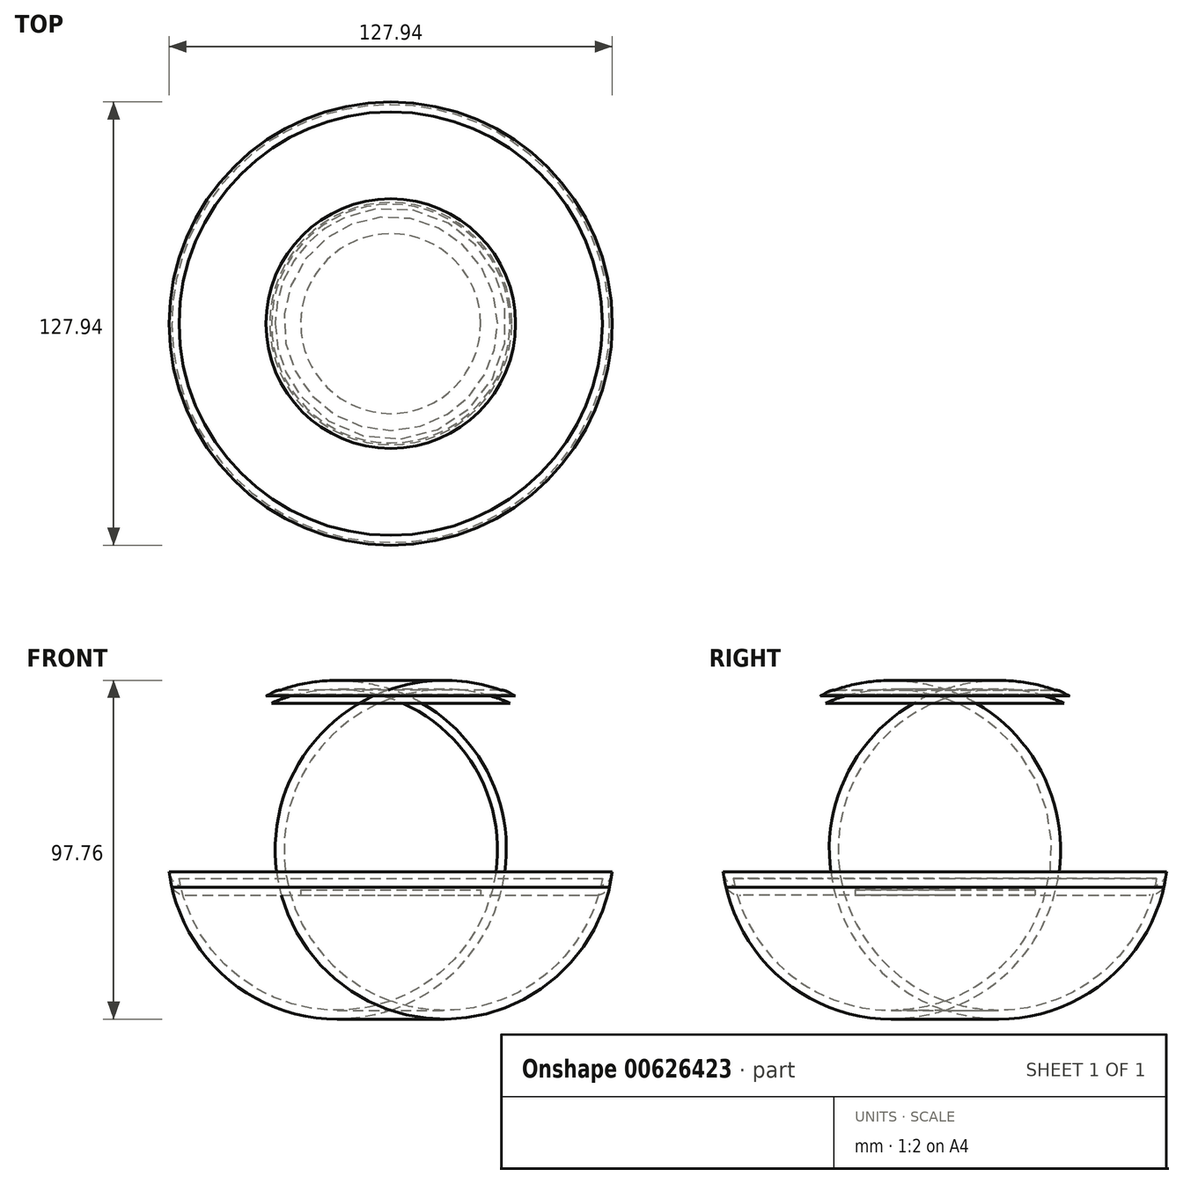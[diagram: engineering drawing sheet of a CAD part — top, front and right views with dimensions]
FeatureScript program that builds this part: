
annotation { "Feature Type Name" : "Feature", "Feature Type Description" : "" }
export const myFeature = defineFeature(function(context is Context, id is Id, definition is map)
    precondition{}
    {
        {
            var Q0;
            Q0=qCreatedBy(makeId("Front.planeOp"),FACE);
            var sketch = newSketch(context, id + "F0", { "sketchPlane" : qUnion([Q0])});
            skLineSegment(sketch, "E0", {"start": v(-34.97, 0) * mm, "end": v(37.56, 0) * mm});
            skLineSegment(sketch, "E1", {"start": v(-63.17, -55.7) * mm, "end": v(68.93, -55.7) * mm});
            skArc(sketch, "E2", {"start": v(-34.97, 0) * mm, "mid": v(-59.12, -22.76) * mm, "end": v(-63.17, -55.7) * mm});
            skArc(sketch, "E3", {"start": v(68.93, -55.7) * mm, "mid": v(64.02, -21.78) * mm, "end": v(37.56, 0) * mm});
            skLineSegment(sketch, "E4", {"start": v(0, 0) * mm, "end": v(0, -55.7) * mm});
            skSolve(sketch);
        }
        {
            var Q0;
            {var subQ0=sQuery(id+"F0.wireOp",EDGE,"E2");Q0=makeQuery(id+"F0.imprint","IMPRINT",FACE,{"disambiguationData":[TD([[makeQuery(id+"F0.imprint","IMPRINT",EDGE,{"derivedFrom":subQ0}),1.0]])]});}
            var Q1;
            Q1=sQuery(id+"F0.wireOp",EDGE,"E4");
            revolve(context, id + "F1", {"entities" : qUnion([Q0]), "axis" : qUnion([Q1]), "revolveType" : RevolveType.FULL});
        }
        {
            var Q0;
            Q0=makeQuery(id+"F1.opRevolve","SWEPT_FACE",FACE,{"disambiguationData":[OSD([sQuery(id+"F0.wireOp",EDGE,"E0")])]});
            var sketch = newSketch(context, id + "F2", { "sketchPlane" : qUnion([Q0])});
            skCircle(sketch, "E5", {"center": v(0, 0) * mm, "radius": 34.94 * mm});
            skSolve(sketch);
        }
        {
            var Q0;
            Q0=makeQuery(id+"F2.imprint","IMPRINT",FACE,{"disambiguationData":[TD([[makeQuery(id+"F2.imprint","IMPRINT",EDGE,{"derivedFrom":sQuery(id+"F2.wireOp",EDGE,"E5")}),1.0]])]});
            extrude(context, id + "F3", {"entities" : qUnion([Q0]), "depth" : 1.27 * mm, "offsetDistance" : 25.4 * mm});
        }
        {
            var Q0;
            Q0=makeQuery(id+"F1.opRevolve","SWEPT_FACE",FACE,{"disambiguationData":[OSD([sQuery(id+"F0.wireOp",EDGE,"E1")])]});
            var sketch = newSketch(context, id + "F4", { "sketchPlane" : qUnion([Q0])});
            skCircle(sketch, "E6", {"center": v(0, 0) * mm, "radius": 63.53 * mm});
            skSolve(sketch);
        }
        {
            var Q0;
            Q0=makeQuery(id+"F4.imprint","IMPRINT",FACE,{"disambiguationData":[TD([[makeQuery(id+"F4.imprint","IMPRINT",EDGE,{"derivedFrom":makeQuery(id+"F1.opRevolve","SWEPT_EDGE",EDGE,{"disambiguationData":[OSD([sQuery(id+"F0.wireOp",EDGE,"E1"),sQuery(id+"F0.wireOp",EDGE,"E2")])]})}),-1.0]])]});
            extrude(context, id + "F5", {"entities" : qUnion([Q0]), "depth" : 2.3 * mm, "offsetDistance" : 25.4 * mm});
        }
        {
            var Q0;
            Q0=makeQuery(id+"F1.opRevolve","SWEPT_FACE",FACE,{"disambiguationData":[OSD([sQuery(id+"F0.wireOp",EDGE,"E2")])]});
            var Q1;
            Q1=makeQuery(id+"F1.opRevolve","SWEPT_BODY",BODY,{"disambiguationData":[OSD([sQuery(id+"F0.wireOp",EDGE,"E0"),sQuery(id+"F0.wireOp",EDGE,"E1"),sQuery(id+"F0.wireOp",EDGE,"E2"),sQuery(id+"F0.wireOp",EDGE,"E4")])]});
            shell(context, id + "F6", {"isHollow" : true, "entities" : qUnion([Q0]), "parts" : qUnion([Q1]), "thickness" : 2.54 * mm});
        }
        {
            var Q0;
            Q0=makeQuery(id+"F5.opExtrude","CAP_EDGE",EDGE,{"disambiguationData":[OSD([sQuery(id+"F0.wireOp",EDGE,"E1"),sQuery(id+"F0.wireOp",EDGE,"E2")])],"isStart":false});
            var Q1;
            Q1=makeQuery(id+"F3.opExtrude","CAP_EDGE",EDGE,{"disambiguationData":[OSD([sQuery(id+"F2.wireOp",EDGE,"E5")])],"isStart":false});
            var Q2;
            Q2=makeQuery(id+"F1.opRevolve","SWEPT_EDGE",EDGE,{"disambiguationData":[OSD([sQuery(id+"F0.wireOp",EDGE,"E0"),sQuery(id+"F0.wireOp",EDGE,"E2")])]});
            var Q3;
            Q3=makeQuery(id+"F1.opRevolve","SWEPT_EDGE",EDGE,{"disambiguationData":[OSD([sQuery(id+"F0.wireOp",EDGE,"E1"),sQuery(id+"F0.wireOp",EDGE,"E2")])]});
            fillet(context, id + "F7", {"entities" : qUnion([Q0, Q1, Q2, Q3]), "radius" : 5.08 * mm, "tangentPropagation" : true, "allowEdgeOverflow" : false});
        }
        {
            var Q0;
            Q0=makeQuery(id+"F5.opExtrude","CAP_FACE",FACE,{"disambiguationData":[OSD([sQuery(id+"F0.wireOp",EDGE,"E1"),sQuery(id+"F0.wireOp",EDGE,"E2")])],"isStart":false});
            var sketch = newSketch(context, id + "F8", { "sketchPlane" : qUnion([Q0])});
            skCircle(sketch, "E7", {"center": v(0, 0) * mm, "radius": 25.97 * mm});
            skSolve(sketch);
        }
        {
            var Q0;
            Q0=makeQuery(id+"F8.imprint","IMPRINT",FACE,{"disambiguationData":[TD([[makeQuery(id+"F8.imprint","IMPRINT",EDGE,{"derivedFrom":sQuery(id+"F8.wireOp",EDGE,"E7")}),1.0]])]});
            extrude(context, id + "F9", {"entities" : qUnion([Q0]), "operationType" : NewBodyOperationType.REMOVE, "oppositeDirection" : true, "depth" : 1.52 * mm, "offsetDistance" : 25.4 * mm});
        }
    });
